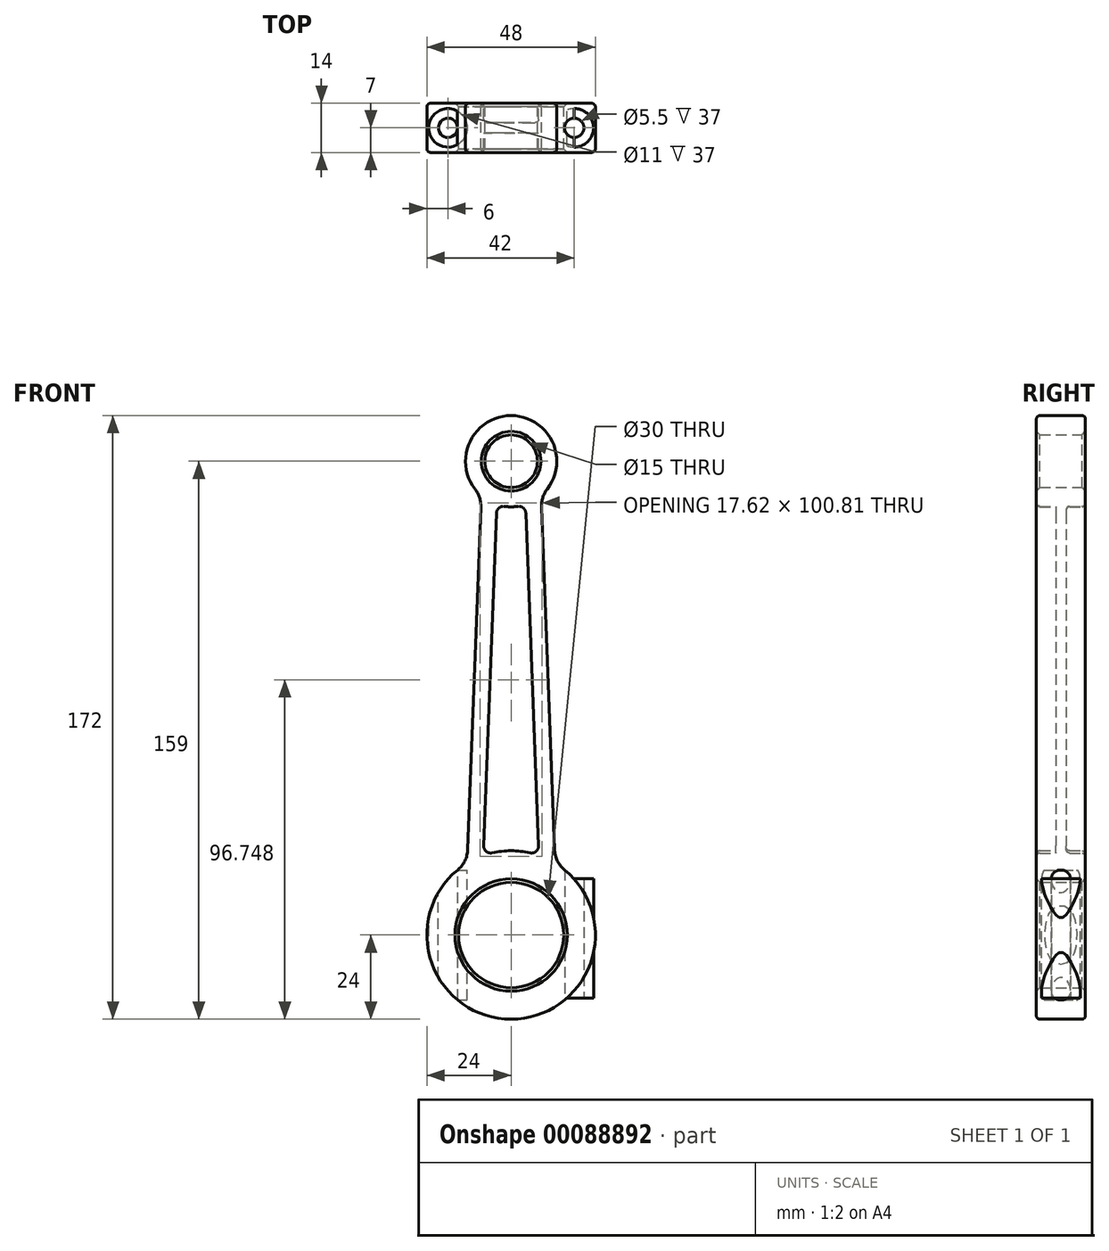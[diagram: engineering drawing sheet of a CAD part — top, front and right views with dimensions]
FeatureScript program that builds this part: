
annotation { "Feature Type Name" : "Feature", "Feature Type Description" : "" }
export const myFeature = defineFeature(function(context is Context, id is Id, definition is map)
    precondition{}
    {
        {
            var Q0;
            Q0=qCreatedBy(makeId("Front.planeOp"),FACE);
            var sketch = newSketch(context, id + "F0", { "sketchPlane" : qUnion([Q0])});
            skCircle(sketch, "E0", {"center": v(0, 0) * mm, "radius": 15 * mm});
            skArc(sketch, "E1", {"start": v(-15.26, 18.52) * mm, "mid": v(0, -24) * mm, "end": v(15.26, 18.52) * mm});
            skCircle(sketch, "E2", {"center": v(0, 135) * mm, "radius": 7.5 * mm});
            skArc(sketch, "E3", {"start": v(-1.9, 122.14) * mm, "mid": v(0, 122) * mm, "end": v(1.9, 122.14) * mm});
            skLineSegment(sketch, "E4", {"start": v(0, 135) * mm, "end": v(0, 0) * mm, "construction": true});
            skLineSegment(sketch, "E5", {"start": v(-8.63, 121.86) * mm, "end": v(-12.35, 24.4) * mm});
            skLineSegment(sketch, "E6.0", {"start": v(-4.19, 120.24) * mm, "end": v(-7.8, 25.42) * mm});
            skLineSegment(sketch, "E7.MirrorCS", {"start": v(4.19, 120.24) * mm, "end": v(7.8, 25.42) * mm});
            skLineSegment(sketch, "E8.MirrorCS", {"start": v(8.63, 121.86) * mm, "end": v(12.35, 24.4) * mm});
            skArc(sketch, "E9.trimOffspring", {"start": v(10.29, 127.05) * mm, "mid": v(0, 148) * mm, "end": v(-10.29, 127.05) * mm});
            skArc(sketch, "E10.trimOffspring", {"start": v(5.36, 23.4) * mm, "mid": v(0, 24) * mm, "end": v(-5.36, 23.4) * mm});
            skPoint(sketch, "E11.visualSharp", {"position": v(8.5, 125.16) * mm});
            skArc(sketch, "E11.filletArc", {"start": v(10.29, 127.05) * mm, "mid": v(9, 124.6) * mm, "end": v(8.63, 121.86) * mm});
            skPoint(sketch, "E12.visualSharp", {"position": v(-8.5, 125.16) * mm});
            skArc(sketch, "E12.filletArc", {"start": v(-8.63, 121.86) * mm, "mid": v(-9, 124.6) * mm, "end": v(-10.29, 127.05) * mm});
            skPoint(sketch, "E13.visualSharp", {"position": v(-12.5, 20.49) * mm});
            skArc(sketch, "E13.filletArc", {"start": v(-15.26, 18.52) * mm, "mid": v(-13.18, 21.15) * mm, "end": v(-12.35, 24.4) * mm});
            skPoint(sketch, "E14.visualSharp", {"position": v(12.5, 20.49) * mm});
            skArc(sketch, "E14.filletArc", {"start": v(12.35, 24.4) * mm, "mid": v(13.18, 21.15) * mm, "end": v(15.26, 18.52) * mm});
            skPoint(sketch, "E15.visualSharp", {"position": v(-4.1, 122.66) * mm});
            skArc(sketch, "E15.filletArc", {"start": v(-1.9, 122.14) * mm, "mid": v(-3.46, 121.7) * mm, "end": v(-4.19, 120.24) * mm});
            skPoint(sketch, "E16.visualSharp", {"position": v(4.1, 122.66) * mm});
            skArc(sketch, "E16.filletArc", {"start": v(4.19, 120.24) * mm, "mid": v(3.46, 121.7) * mm, "end": v(1.9, 122.14) * mm});
            skPoint(sketch, "E17.visualSharp", {"position": v(-7.91, 22.66) * mm});
            skArc(sketch, "E17.filletArc", {"start": v(-7.8, 25.42) * mm, "mid": v(-7.09, 23.8) * mm, "end": v(-5.36, 23.4) * mm});
            skPoint(sketch, "E18.visualSharp", {"position": v(7.91, 22.66) * mm});
            skArc(sketch, "E18.filletArc", {"start": v(5.36, 23.4) * mm, "mid": v(7.09, 23.8) * mm, "end": v(7.8, 25.42) * mm});
            skSolve(sketch);
        }
        {
            var Q0;
            Q0=makeQuery(id+"F0.imprint","IMPRINT",FACE,{"disambiguationData":[TD([[makeQuery(id+"F0.imprint","IMPRINT",EDGE,{"derivedFrom":sQuery(id+"F0.wireOp",EDGE,"E0")}),-1.0]])]});
            extrude(context, id + "F1", {"entities" : qUnion([Q0]), "endBound" : BoundingType.SYMMETRIC, "depth" : 14 * mm});
        }
        {
            var Q0;
            Q0=makeQuery(id+"F0.imprint","IMPRINT",FACE,{"disambiguationData":[TD([[makeQuery(id+"F0.imprint","IMPRINT",EDGE,{"derivedFrom":sQuery(id+"F0.wireOp",EDGE,"E3")}),-1.0]])]});
            extrude(context, id + "F2", {"entities" : qUnion([Q0]), "operationType" : NewBodyOperationType.ADD, "endBound" : BoundingType.SYMMETRIC, "depth" : 3 * mm});
        }
        {
            var Q0;
            Q0=qCreatedBy(makeId("Top.planeOp"),FACE);
            var sketch = newSketch(context, id + "F3", { "sketchPlane" : qUnion([Q0])});
            skCircle(sketch, "E19", {"center": v(18, 0) * mm, "radius": 5.5 * mm});
            skCircle(sketch, "E20", {"center": v(18, 0) * mm, "radius": 2.75 * mm});
            skLineSegment(sketch, "E21", {"start": v(0, 0) * mm, "end": v(0, 7.03) * mm, "construction": true});
            skCircle(sketch, "E22.MirrorC", {"center": v(-18, 0) * mm, "radius": 5.5 * mm});
            skCircle(sketch, "E23.MirrorC", {"center": v(-18, 0) * mm, "radius": 2.75 * mm});
            skSolve(sketch);
        }
        {
            var Q0;
            Q0=makeQuery(id+"F3.imprint","IMPRINT",FACE,{"disambiguationData":[TD([[makeQuery(id+"F3.imprint","IMPRINT",EDGE,{"derivedFrom":sQuery(id+"F3.wireOp",EDGE,"E19")}),1.0]])]});
            var Q1;
            Q1=makeQuery(id+"F3.imprint","IMPRINT",FACE,{"disambiguationData":[TD([[makeQuery(id+"F3.imprint","IMPRINT",EDGE,{"derivedFrom":sQuery(id+"F3.wireOp",EDGE,"E22.MirrorC")}),-1.0]])]});
            extrude(context, id + "F4", {"entities" : qUnion([Q0, Q1]), "operationType" : NewBodyOperationType.ADD, "depth" : 16 * mm});
        }
        {
            var Q0;
            Q0=makeQuery(id+"F3.imprint","IMPRINT",FACE,{"disambiguationData":[TD([[makeQuery(id+"F3.imprint","IMPRINT",EDGE,{"derivedFrom":sQuery(id+"F3.wireOp",EDGE,"E22.MirrorC")}),-1.0]])]});
            var Q1;
            Q1=makeQuery(id+"F3.imprint","IMPRINT",FACE,{"disambiguationData":[TD([[makeQuery(id+"F3.imprint","IMPRINT",EDGE,{"derivedFrom":sQuery(id+"F3.wireOp",EDGE,"E19")}),1.0]])]});
            extrude(context, id + "F5", {"entities" : qUnion([Q0, Q1]), "operationType" : NewBodyOperationType.ADD, "oppositeDirection" : true, "depth" : 18 * mm});
        }
        {
            var Q0;
            Q0=makeQuery(id+"F0.imprint","IMPRINT",FACE,{"disambiguationData":[TD([[makeQuery(id+"F0.imprint","IMPRINT",EDGE,{"derivedFrom":sQuery(id+"F0.wireOp",EDGE,"E0")}),1.0]])]});
            extrude(context, id + "F6", {"entities" : qUnion([Q0]), "operationType" : NewBodyOperationType.REMOVE, "endBound" : BoundingType.SYMMETRIC, "oppositeDirection" : true, "depth" : 25 * mm});
        }
        {
            var Q0;
            Q0=makeQuery(id+"F3.imprint","IMPRINT",FACE,{"disambiguationData":[TD([[makeQuery(id+"F3.imprint","IMPRINT",EDGE,{"derivedFrom":sQuery(id+"F3.wireOp",EDGE,"E23.MirrorC")}),-1.0]])]});
            var Q1;
            Q1=makeQuery(id+"F3.imprint","IMPRINT",FACE,{"disambiguationData":[TD([[makeQuery(id+"F3.imprint","IMPRINT",EDGE,{"derivedFrom":sQuery(id+"F3.wireOp",EDGE,"E20")}),1.0]])]});
            extrude(context, id + "F7", {"entities" : qUnion([Q0, Q1]), "operationType" : NewBodyOperationType.REMOVE, "endBound" : BoundingType.SYMMETRIC, "oppositeDirection" : true, "depth" : 37 * mm});
        }
        {
            var Q0;
            Q0=makeQuery(id+"F1.opExtrude","CAP_EDGE",EDGE,{"disambiguationData":[OSD([sQuery(id+"F0.wireOp",EDGE,"E2")])],"isStart":false});
            var Q1;
            Q1=makeQuery(id+"F1.opExtrude","CAP_EDGE",EDGE,{"disambiguationData":[OSD([sQuery(id+"F0.wireOp",EDGE,"E2")])],"isStart":true});
            var Q2;
            Q2=makeQuery(id+"F1.opExtrude","CAP_EDGE",EDGE,{"disambiguationData":[OSD([sQuery(id+"F0.wireOp",EDGE,"E0")])],"isStart":false});
            var Q3;
            Q3=makeQuery(id+"F1.opExtrude","CAP_EDGE",EDGE,{"disambiguationData":[OSD([sQuery(id+"F0.wireOp",EDGE,"E0")])],"isStart":true});
            chamfer(context, id + "F8", {"entities" : qUnion([Q0, Q1, Q2, Q3]), "width" : 1 * mm, "tangentPropagation" : true});
        }
        {
            var Q0;
            Q0=makeQuery(id+"F1.opExtrude","CAP_EDGE",EDGE,{"disambiguationData":[OSD([sQuery(id+"F0.wireOp",EDGE,"E6.0")])],"isStart":false});
            var Q1;
            Q1=makeQuery(id+"F1.opExtrude","CAP_EDGE",EDGE,{"disambiguationData":[OSD([sQuery(id+"F0.wireOp",EDGE,"E6.0")])],"isStart":true});
            var Q2;
            Q2=makeQuery(id+"F2.opExtrude","CAP_EDGE",EDGE,{"disambiguationData":[OSD([sQuery(id+"F0.wireOp",EDGE,"E6.0")])],"isStart":true});
            var Q3;
            Q3=makeQuery(id+"F2.opExtrude","CAP_EDGE",EDGE,{"disambiguationData":[OSD([sQuery(id+"F0.wireOp",EDGE,"E6.0")])],"isStart":false});
            fillet(context, id + "F9", {"entities" : qUnion([Q0, Q1, Q2, Q3]), "radius" : 1 * mm, "tangentPropagation" : true, "allowEdgeOverflow" : false});
        }
        {
            var Q0;
            Q0=makeQuery(id+"F1.opExtrude","CAP_EDGE",EDGE,{"disambiguationData":[OSD([sQuery(id+"F0.wireOp",EDGE,"E8.MirrorCS")])],"isStart":false});
            var Q1;
            Q1=makeQuery(id+"F1.opExtrude","CAP_EDGE",EDGE,{"disambiguationData":[OSD([sQuery(id+"F0.wireOp",EDGE,"E8.MirrorCS")])],"isStart":true});
            fillet(context, id + "F10", {"entities" : qUnion([Q0, Q1]), "radius" : 1 * mm, "tangentPropagation" : true, "allowEdgeOverflow" : false});
        }
    });
